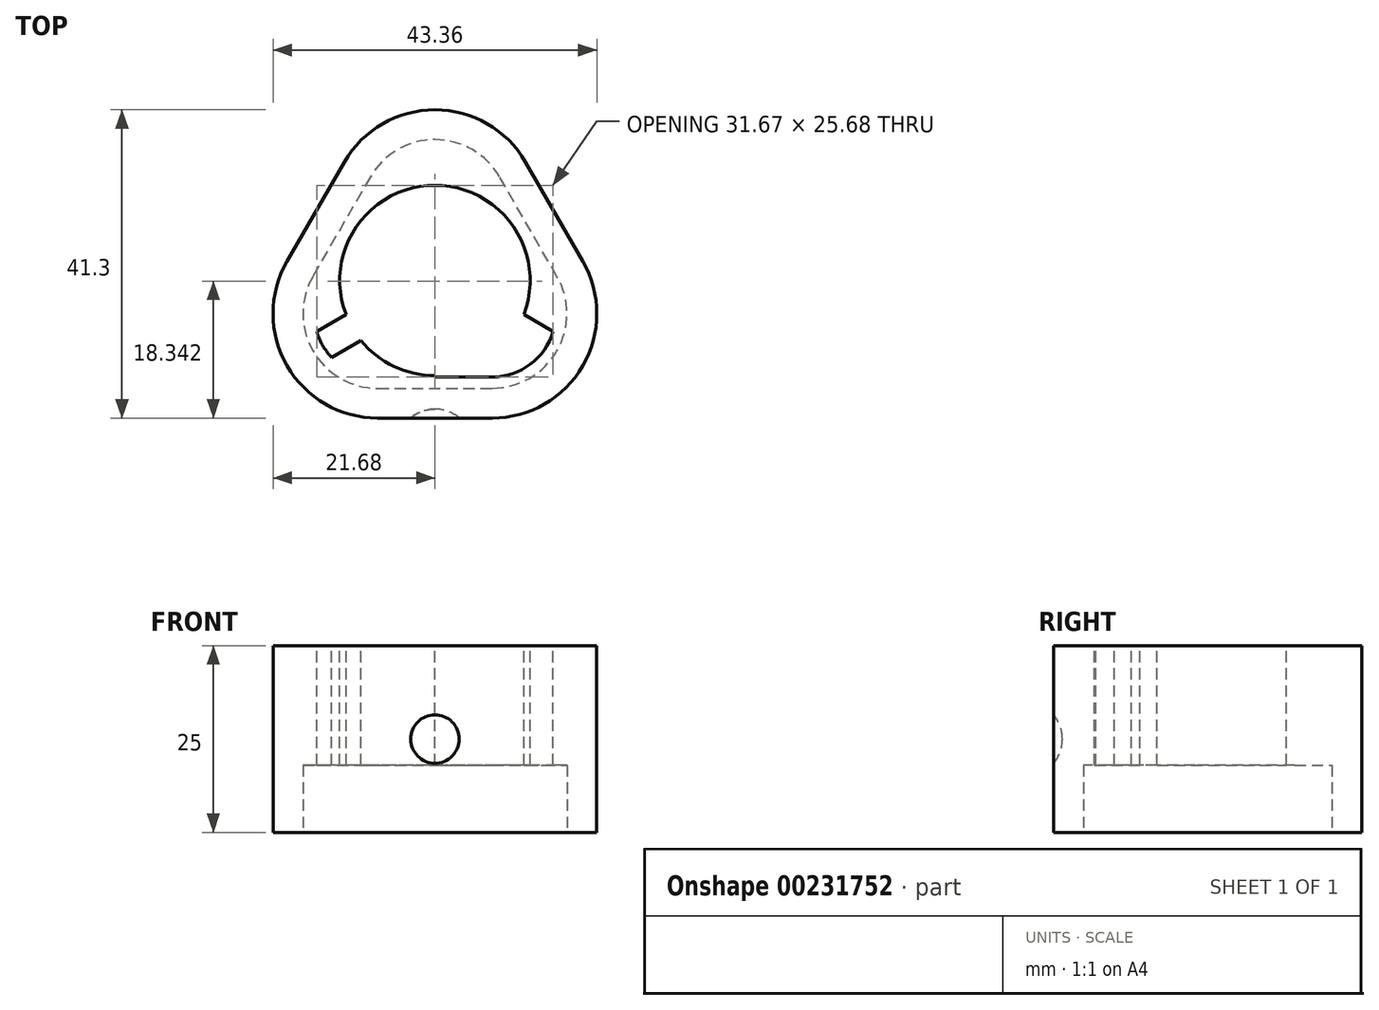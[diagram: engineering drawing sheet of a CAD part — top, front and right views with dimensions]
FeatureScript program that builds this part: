
annotation { "Feature Type Name" : "Feature", "Feature Type Description" : "" }
export const myFeature = defineFeature(function(context is Context, id is Id, definition is map)
    precondition{}
    {
        {
            var Q0;
            Q0=qCreatedBy(makeId("Top.planeOp"),FACE);
            var sketch = newSketch(context, id + "F0", { "sketchPlane" : qUnion([Q0])});
            skLineSegment(sketch, "E0", {"start": v(0, 0) * mm, "end": v(7.68, 0) * mm});
            skLineSegment(sketch, "E1", {"start": v(16.34, 15) * mm, "end": v(8.66, 28.3) * mm});
            skLineSegment(sketch, "E2", {"start": v(-8.66, 28.3) * mm, "end": v(-16.34, 15) * mm});
            skLineSegment(sketch, "E3", {"start": v(-7.68, 0) * mm, "end": v(0, 0) * mm});
            skLineSegment(sketch, "E4", {"start": v(0, 0) * mm, "end": v(0, 43.3) * mm, "construction": true});
            skLineSegment(sketch, "E5", {"start": v(-12.5, 21.65) * mm, "end": v(25, 0) * mm, "construction": true});
            skLineSegment(sketch, "E6", {"start": v(12.5, 21.65) * mm, "end": v(-25, 0) * mm, "construction": true});
            skCircle(sketch, "E7", {"center": v(0, 14.43) * mm, "radius": 12.5 * mm});
            skPoint(sketch, "E8.visualSharp", {"position": v(0, 43.3) * mm});
            skArc(sketch, "E8.filletArc", {"start": v(8.66, 28.3) * mm, "mid": v(0, 33.3) * mm, "end": v(-8.66, 28.3) * mm});
            skPoint(sketch, "E9.visualSharp", {"position": v(-25, 0) * mm});
            skArc(sketch, "E9.filletArc", {"start": v(-16.34, 15) * mm, "mid": v(-16.34, 5) * mm, "end": v(-7.68, 0) * mm});
            skPoint(sketch, "E10.visualSharp", {"position": v(25, 0) * mm});
            skArc(sketch, "E10.filletArc", {"start": v(7.68, 0) * mm, "mid": v(16.34, 5) * mm, "end": v(16.34, 15) * mm});
            skLineSegment(sketch, "E11.0", {"start": v(19.8, 17) * mm, "end": v(12.12, 30.3) * mm});
            skArc(sketch, "E11.1", {"start": v(7.68, -4) * mm, "mid": v(19.8, 3) * mm, "end": v(19.8, 17) * mm});
            skLineSegment(sketch, "E11.2", {"start": v(-12.12, 30.3) * mm, "end": v(-19.8, 17) * mm});
            skArc(sketch, "E11.3", {"start": v(-19.8, 17) * mm, "mid": v(-19.8, 3) * mm, "end": v(-7.68, -4) * mm});
            skLineSegment(sketch, "E11.4", {"start": v(-7.68, -4) * mm, "end": v(0, -4) * mm});
            skArc(sketch, "E11.5", {"start": v(12.12, 30.3) * mm, "mid": v(0, 37.3) * mm, "end": v(-12.12, 30.3) * mm});
            skLineSegment(sketch, "E11.6", {"start": v(0, -4) * mm, "end": v(7.68, -4) * mm});
            skSolve(sketch);
        }
        {
            var Q0;
            Q0=makeQuery(id+"F0.imprint","IMPRINT",FACE,{"disambiguationData":[TD([[makeQuery(id+"F0.imprint","IMPRINT",EDGE,{"derivedFrom":sQuery(id+"F0.wireOp",EDGE,"E0")}),-1.0]])]});
            extrude(context, id + "F1", {"entities" : qUnion([Q0]), "depth" : 25 * mm});
        }
        {
            var Q0;
            Q0=makeQuery(id+"F1.opExtrude","CAP_FACE",FACE,{"disambiguationData":[OSD([sQuery(id+"F0.wireOp",EDGE,"E0"),sQuery(id+"F0.wireOp",EDGE,"E1"),sQuery(id+"F0.wireOp",EDGE,"E2"),sQuery(id+"F0.wireOp",EDGE,"E3"),sQuery(id+"F0.wireOp",EDGE,"E8.filletArc"),sQuery(id+"F0.wireOp",EDGE,"E9.filletArc"),sQuery(id+"F0.wireOp",EDGE,"E10.filletArc"),sQuery(id+"F0.wireOp",EDGE,"E11.0"),sQuery(id+"F0.wireOp",EDGE,"E11.1"),sQuery(id+"F0.wireOp",EDGE,"E11.2"),sQuery(id+"F0.wireOp",EDGE,"E11.3"),sQuery(id+"F0.wireOp",EDGE,"E11.4"),sQuery(id+"F0.wireOp",EDGE,"E11.5"),sQuery(id+"F0.wireOp",EDGE,"E11.6")])],"isStart":false});
            var sketch = newSketch(context, id + "F2", { "sketchPlane" : qUnion([Q0])});
            skLineSegment(sketch, "E12", {"start": v(-12.5, 21.65) * mm, "end": v(16.34, 5) * mm});
            skLineSegment(sketch, "E13", {"start": v(12.5, 21.65) * mm, "end": v(-16.34, 5) * mm});
            skCircle(sketch, "E14", {"center": v(0, 14.43) * mm, "radius": 12.75 * mm});
            skLineSegment(sketch, "E15.0", {"start": v(-8.66, 28.3) * mm, "end": v(-16.34, 15) * mm});
            skArc(sketch, "E16.0", {"start": v(-16.34, 15) * mm, "mid": v(-16.34, 5) * mm, "end": v(-7.68, 0) * mm});
            skLineSegment(sketch, "E17.0", {"start": v(-7.68, 0) * mm, "end": v(7.68, 0) * mm});
            skArc(sketch, "E18.0", {"start": v(7.68, 0) * mm, "mid": v(16.34, 5) * mm, "end": v(16.34, 15) * mm});
            skLineSegment(sketch, "E19.0", {"start": v(16.34, 15) * mm, "end": v(8.66, 28.3) * mm});
            skArc(sketch, "E20.0", {"start": v(8.66, 28.3) * mm, "mid": v(0, 33.3) * mm, "end": v(-8.66, 28.3) * mm});
            skLineSegment(sketch, "E21.0", {"start": v(11.5, 23.38) * mm, "end": v(-17.34, 6.73) * mm});
            skLineSegment(sketch, "E22.0", {"start": v(13.5, 19.92) * mm, "end": v(-15.34, 3.27) * mm});
            skLineSegment(sketch, "E23.0", {"start": v(-13.5, 19.92) * mm, "end": v(15.34, 3.27) * mm});
            skLineSegment(sketch, "E24.0", {"start": v(-11.5, 23.38) * mm, "end": v(17.34, 6.73) * mm});
            skLineSegment(sketch, "E25", {"start": v(0, 0) * mm, "end": v(0, 33.3) * mm});
            skLineSegment(sketch, "E26.0", {"start": v(2, 0) * mm, "end": v(2, 33.3) * mm});
            skLineSegment(sketch, "E27.0", {"start": v(-2, 0) * mm, "end": v(-2, 33.3) * mm});
            skArc(sketch, "E28.0", {"start": v(7.36, 27.55) * mm, "mid": v(0, 31.8) * mm, "end": v(-7.36, 27.55) * mm});
            skArc(sketch, "E28.1", {"start": v(-15.04, 14.25) * mm, "mid": v(-15.04, 5.75) * mm, "end": v(-7.68, 1.5) * mm});
            skLineSegment(sketch, "E28.2", {"start": v(-7.68, 1.5) * mm, "end": v(7.68, 1.5) * mm});
            skLineSegment(sketch, "E28.3", {"start": v(-7.36, 27.55) * mm, "end": v(-15.04, 14.25) * mm});
            skArc(sketch, "E28.4", {"start": v(7.68, 1.5) * mm, "mid": v(15.04, 5.75) * mm, "end": v(15.04, 14.25) * mm});
            skLineSegment(sketch, "E28.5", {"start": v(15.04, 14.25) * mm, "end": v(7.36, 27.55) * mm});
            skSolve(sketch);
        }
        {
            var Q0;
            {var subQ0=sQuery(id+"F2.wireOp",EDGE,"E15.0");var subQ1=sQuery(id+"F2.wireOp",EDGE,"E12");var subQ2=makeQuery(id+"F2.imprint","INTERSECT",VERTEX,{"derivedFrom":[subQ1,subQ0]});Q0=makeQuery(id+"F2.imprint","IMPRINT",FACE,{"disambiguationData":[TD([[makeQuery(id+"F2.imprint","IMPRINT",EDGE,{"disambiguationData":[TD([[subQ2,-1.0]])],"derivedFrom":subQ1}),1.0]])]});}
            var Q1;
            {var subQ0=sQuery(id+"F2.wireOp",EDGE,"E15.0");var subQ1=sQuery(id+"F2.wireOp",EDGE,"E12");var subQ2=makeQuery(id+"F2.imprint","INTERSECT",VERTEX,{"derivedFrom":[subQ1,subQ0]});Q1=makeQuery(id+"F2.imprint","IMPRINT",FACE,{"disambiguationData":[TD([[makeQuery(id+"F2.imprint","IMPRINT",EDGE,{"disambiguationData":[TD([[subQ2,-1.0]])],"derivedFrom":subQ1}),-1.0]])]});}
            var Q2;
            {var subQ0=sQuery(id+"F2.wireOp",EDGE,"E18.0");var subQ1=sQuery(id+"F2.wireOp",EDGE,"E12");var subQ2=makeQuery(id+"F2.imprint","INTERSECT",VERTEX,{"derivedFrom":[subQ1,subQ0]});Q2=makeQuery(id+"F2.imprint","IMPRINT",FACE,{"disambiguationData":[TD([[makeQuery(id+"F2.imprint","IMPRINT",EDGE,{"disambiguationData":[TD([[subQ2,1.0]])],"derivedFrom":subQ1}),-1.0]])]});}
            var Q3;
            {var subQ0=sQuery(id+"F2.wireOp",EDGE,"E18.0");var subQ1=sQuery(id+"F2.wireOp",EDGE,"E12");var subQ2=makeQuery(id+"F2.imprint","INTERSECT",VERTEX,{"derivedFrom":[subQ1,subQ0]});Q3=makeQuery(id+"F2.imprint","IMPRINT",FACE,{"disambiguationData":[TD([[makeQuery(id+"F2.imprint","IMPRINT",EDGE,{"disambiguationData":[TD([[subQ2,1.0]])],"derivedFrom":subQ1}),1.0]])]});}
            var Q4;
            {var subQ0=sQuery(id+"F2.wireOp",EDGE,"E19.0");var subQ1=sQuery(id+"F2.wireOp",EDGE,"E13");var subQ2=makeQuery(id+"F2.imprint","INTERSECT",VERTEX,{"derivedFrom":[subQ1,subQ0]});Q4=makeQuery(id+"F2.imprint","IMPRINT",FACE,{"disambiguationData":[TD([[makeQuery(id+"F2.imprint","IMPRINT",EDGE,{"disambiguationData":[TD([[subQ2,-1.0]])],"derivedFrom":subQ1}),1.0]])]});}
            var Q5;
            {var subQ0=sQuery(id+"F2.wireOp",EDGE,"E19.0");var subQ1=sQuery(id+"F2.wireOp",EDGE,"E13");var subQ2=makeQuery(id+"F2.imprint","INTERSECT",VERTEX,{"derivedFrom":[subQ1,subQ0]});Q5=makeQuery(id+"F2.imprint","IMPRINT",FACE,{"disambiguationData":[TD([[makeQuery(id+"F2.imprint","IMPRINT",EDGE,{"disambiguationData":[TD([[subQ2,-1.0]])],"derivedFrom":subQ1}),-1.0]])]});}
            var Q6;
            {var subQ0=sQuery(id+"F2.wireOp",EDGE,"E16.0");var subQ1=sQuery(id+"F2.wireOp",EDGE,"E13");var subQ2=makeQuery(id+"F2.imprint","INTERSECT",VERTEX,{"derivedFrom":[subQ1,subQ0]});Q6=makeQuery(id+"F2.imprint","IMPRINT",FACE,{"disambiguationData":[TD([[makeQuery(id+"F2.imprint","IMPRINT",EDGE,{"disambiguationData":[TD([[subQ2,1.0]])],"derivedFrom":subQ1}),-1.0]])]});}
            var Q7;
            {var subQ0=sQuery(id+"F2.wireOp",EDGE,"E16.0");var subQ1=sQuery(id+"F2.wireOp",EDGE,"E13");var subQ2=makeQuery(id+"F2.imprint","INTERSECT",VERTEX,{"derivedFrom":[subQ1,subQ0]});Q7=makeQuery(id+"F2.imprint","IMPRINT",FACE,{"disambiguationData":[TD([[makeQuery(id+"F2.imprint","IMPRINT",EDGE,{"disambiguationData":[TD([[subQ2,1.0]])],"derivedFrom":subQ1}),1.0]])]});}
            var Q8;
            {var subQ1=sQuery(id+"F2.wireOp",EDGE,"E20.0");var subQ9=sQuery(id+"F2.wireOp",EDGE,"E15.0");var subQ11=makeQuery(id+"F2.imprint","INTERSECT",VERTEX,{"derivedFrom":[subQ9,subQ1]});Q8=makeQuery(id+"F2.imprint","IMPRINT",FACE,{"disambiguationData":[TD([[makeQuery(id+"F2.imprint","IMPRINT",EDGE,{"disambiguationData":[TD([[subQ11,-1.0]])],"derivedFrom":subQ9}),1.0]])]});}
            var Q9;
            {var subQ1=sQuery(id+"F2.wireOp",EDGE,"E15.0");var subQ9=sQuery(id+"F2.wireOp",EDGE,"E16.0");var subQ11=makeQuery(id+"F2.imprint","INTERSECT",VERTEX,{"derivedFrom":[subQ1,subQ9]});Q9=makeQuery(id+"F2.imprint","IMPRINT",FACE,{"disambiguationData":[TD([[makeQuery(id+"F2.imprint","IMPRINT",EDGE,{"disambiguationData":[TD([[subQ11,1.0]])],"derivedFrom":subQ1}),1.0]])]});}
            var Q10;
            {var subQ1=sQuery(id+"F2.wireOp",EDGE,"E16.0");var subQ5=sQuery(id+"F2.wireOp",EDGE,"E17.0");var subQ6=makeQuery(id+"F2.imprint","INTERSECT",VERTEX,{"derivedFrom":[subQ1,subQ5]});Q10=makeQuery(id+"F2.imprint","IMPRINT",FACE,{"disambiguationData":[TD([[makeQuery(id+"F2.imprint","IMPRINT",EDGE,{"disambiguationData":[TD([[subQ6,1.0]])],"derivedFrom":subQ1}),1.0]])]});}
            var Q11;
            {var subQ0=sQuery(id+"F2.wireOp",EDGE,"E25");var subQ1=sQuery(id+"F2.wireOp",EDGE,"E17.0");var subQ2=makeQuery(id+"F2.imprint","INTERSECT",VERTEX,{"derivedFrom":[subQ1,subQ0]});Q11=makeQuery(id+"F2.imprint","IMPRINT",FACE,{"disambiguationData":[TD([[makeQuery(id+"F2.imprint","IMPRINT",EDGE,{"disambiguationData":[TD([[subQ2,1.0]])],"derivedFrom":subQ1}),1.0]])]});}
            var Q12;
            {var subQ0=sQuery(id+"F2.wireOp",EDGE,"E25");var subQ1=sQuery(id+"F2.wireOp",EDGE,"E17.0");var subQ2=makeQuery(id+"F2.imprint","INTERSECT",VERTEX,{"derivedFrom":[subQ1,subQ0]});Q12=makeQuery(id+"F2.imprint","IMPRINT",FACE,{"disambiguationData":[TD([[makeQuery(id+"F2.imprint","IMPRINT",EDGE,{"disambiguationData":[TD([[subQ2,-1.0]])],"derivedFrom":subQ1}),1.0]])]});}
            var Q13;
            {var subQ1=sQuery(id+"F2.wireOp",EDGE,"E17.0");var subQ9=sQuery(id+"F2.wireOp",EDGE,"E18.0");var subQ10=makeQuery(id+"F2.imprint","INTERSECT",VERTEX,{"derivedFrom":[subQ1,subQ9]});Q13=makeQuery(id+"F2.imprint","IMPRINT",FACE,{"disambiguationData":[TD([[makeQuery(id+"F2.imprint","IMPRINT",EDGE,{"disambiguationData":[TD([[subQ10,1.0]])],"derivedFrom":subQ1}),1.0]])]});}
            var Q14;
            {var subQ1=sQuery(id+"F2.wireOp",EDGE,"E18.0");var subQ6=sQuery(id+"F2.wireOp",EDGE,"E19.0");var subQ10=makeQuery(id+"F2.imprint","INTERSECT",VERTEX,{"derivedFrom":[subQ1,subQ6]});Q14=makeQuery(id+"F2.imprint","IMPRINT",FACE,{"disambiguationData":[TD([[makeQuery(id+"F2.imprint","IMPRINT",EDGE,{"disambiguationData":[TD([[subQ10,1.0]])],"derivedFrom":subQ1}),1.0]])]});}
            var Q15;
            {var subQ1=sQuery(id+"F2.wireOp",EDGE,"E20.0");var subQ6=sQuery(id+"F2.wireOp",EDGE,"E19.0");var subQ10=makeQuery(id+"F2.imprint","INTERSECT",VERTEX,{"derivedFrom":[subQ6,subQ1]});Q15=makeQuery(id+"F2.imprint","IMPRINT",FACE,{"disambiguationData":[TD([[makeQuery(id+"F2.imprint","IMPRINT",EDGE,{"disambiguationData":[TD([[subQ10,1.0]])],"derivedFrom":subQ6}),1.0]])]});}
            var Q16;
            {var subQ0=sQuery(id+"F2.wireOp",EDGE,"E25");var subQ1=sQuery(id+"F2.wireOp",EDGE,"E20.0");var subQ2=makeQuery(id+"F2.imprint","INTERSECT",VERTEX,{"derivedFrom":[subQ1,subQ0]});Q16=makeQuery(id+"F2.imprint","IMPRINT",FACE,{"disambiguationData":[TD([[makeQuery(id+"F2.imprint","IMPRINT",EDGE,{"disambiguationData":[TD([[subQ2,1.0]])],"derivedFrom":subQ1}),1.0]])]});}
            var Q17;
            {var subQ0=sQuery(id+"F2.wireOp",EDGE,"E25");var subQ1=sQuery(id+"F2.wireOp",EDGE,"E20.0");var subQ2=makeQuery(id+"F2.imprint","INTERSECT",VERTEX,{"derivedFrom":[subQ1,subQ0]});Q17=makeQuery(id+"F2.imprint","IMPRINT",FACE,{"disambiguationData":[TD([[makeQuery(id+"F2.imprint","IMPRINT",EDGE,{"disambiguationData":[TD([[subQ2,-1.0]])],"derivedFrom":subQ1}),1.0]])]});}
            var Q18;
            {var subQ5=sQuery(id+"F2.wireOp",EDGE,"E23.0");var subQ6=sQuery(id+"F2.wireOp",EDGE,"E14");var subQ7=makeQuery(id+"F2.imprint","INTERSECT",VERTEX,{"disambiguationData":[OD(0.0)],"derivedFrom":[subQ6,subQ5]});Q18=makeQuery(id+"F2.imprint","IMPRINT",FACE,{"disambiguationData":[TD([[makeQuery(id+"F2.imprint","IMPRINT",EDGE,{"disambiguationData":[TD([[subQ7,-1.0]])],"derivedFrom":subQ6}),-1.0]])]});}
            var Q19;
            {var subQ3=sQuery(id+"F2.wireOp",EDGE,"E22.0");var subQ5=sQuery(id+"F2.wireOp",EDGE,"E14");var subQ6=makeQuery(id+"F2.imprint","INTERSECT",VERTEX,{"disambiguationData":[OD(1.0)],"derivedFrom":[subQ5,subQ3]});Q19=makeQuery(id+"F2.imprint","IMPRINT",FACE,{"disambiguationData":[TD([[makeQuery(id+"F2.imprint","IMPRINT",EDGE,{"disambiguationData":[TD([[subQ6,-1.0]])],"derivedFrom":subQ5}),-1.0]])]});}
            var Q20;
            {var subQ1=sQuery(id+"F2.wireOp",EDGE,"E14");var subQ7=sQuery(id+"F2.wireOp",EDGE,"E26.0");var subQ9=makeQuery(id+"F2.imprint","INTERSECT",VERTEX,{"disambiguationData":[OD(1.0)],"derivedFrom":[subQ1,subQ7]});Q20=makeQuery(id+"F2.imprint","IMPRINT",FACE,{"disambiguationData":[TD([[makeQuery(id+"F2.imprint","IMPRINT",EDGE,{"disambiguationData":[TD([[subQ9,-1.0]])],"derivedFrom":subQ1}),-1.0]])]});}
            var Q21;
            {var subQ5=sQuery(id+"F2.wireOp",EDGE,"E14");var subQ7=sQuery(id+"F2.wireOp",EDGE,"E22.0");var subQ8=makeQuery(id+"F2.imprint","INTERSECT",VERTEX,{"disambiguationData":[OD(0.0)],"derivedFrom":[subQ5,subQ7]});Q21=makeQuery(id+"F2.imprint","IMPRINT",FACE,{"disambiguationData":[TD([[makeQuery(id+"F2.imprint","IMPRINT",EDGE,{"disambiguationData":[TD([[subQ8,1.0]])],"derivedFrom":subQ5}),-1.0]])]});}
            var Q22;
            {var subQ1=sQuery(id+"F2.wireOp",EDGE,"E14");var subQ5=sQuery(id+"F2.wireOp",EDGE,"E21.0");var subQ6=makeQuery(id+"F2.imprint","INTERSECT",VERTEX,{"disambiguationData":[OD(0.0)],"derivedFrom":[subQ1,subQ5]});Q22=makeQuery(id+"F2.imprint","IMPRINT",FACE,{"disambiguationData":[TD([[makeQuery(id+"F2.imprint","IMPRINT",EDGE,{"disambiguationData":[TD([[subQ6,-1.0]])],"derivedFrom":subQ1}),-1.0]])]});}
            var Q23;
            {var subQ0=sQuery(id+"F2.wireOp",EDGE,"E27.0");var subQ1=sQuery(id+"F2.wireOp",EDGE,"E14");var subQ2=makeQuery(id+"F2.imprint","INTERSECT",VERTEX,{"disambiguationData":[OD(0.0)],"derivedFrom":[subQ1,subQ0]});Q23=makeQuery(id+"F2.imprint","IMPRINT",FACE,{"disambiguationData":[TD([[makeQuery(id+"F2.imprint","IMPRINT",EDGE,{"disambiguationData":[TD([[subQ2,-1.0]])],"derivedFrom":subQ1}),-1.0]])]});}
            var Q24;
            {var subQ0=sQuery(id+"F2.wireOp",EDGE,"E28.3");var subQ1=sQuery(id+"F2.wireOp",EDGE,"E12");var subQ2=makeQuery(id+"F2.imprint","INTERSECT",VERTEX,{"derivedFrom":[subQ1,subQ0]});Q24=makeQuery(id+"F2.imprint","IMPRINT",FACE,{"disambiguationData":[TD([[makeQuery(id+"F2.imprint","IMPRINT",EDGE,{"disambiguationData":[TD([[subQ2,-1.0]])],"derivedFrom":subQ1}),1.0]])]});}
            var Q25;
            {var subQ0=sQuery(id+"F2.wireOp",EDGE,"E28.3");var subQ1=sQuery(id+"F2.wireOp",EDGE,"E12");var subQ2=makeQuery(id+"F2.imprint","INTERSECT",VERTEX,{"derivedFrom":[subQ1,subQ0]});Q25=makeQuery(id+"F2.imprint","IMPRINT",FACE,{"disambiguationData":[TD([[makeQuery(id+"F2.imprint","IMPRINT",EDGE,{"disambiguationData":[TD([[subQ2,-1.0]])],"derivedFrom":subQ1}),-1.0]])]});}
            var Q26;
            {var subQ0=sQuery(id+"F2.wireOp",EDGE,"E28.5");var subQ1=sQuery(id+"F2.wireOp",EDGE,"E13");var subQ2=makeQuery(id+"F2.imprint","INTERSECT",VERTEX,{"derivedFrom":[subQ1,subQ0]});Q26=makeQuery(id+"F2.imprint","IMPRINT",FACE,{"disambiguationData":[TD([[makeQuery(id+"F2.imprint","IMPRINT",EDGE,{"disambiguationData":[TD([[subQ2,-1.0]])],"derivedFrom":subQ1}),-1.0]])]});}
            var Q27;
            {var subQ0=sQuery(id+"F2.wireOp",EDGE,"E28.5");var subQ1=sQuery(id+"F2.wireOp",EDGE,"E13");var subQ2=makeQuery(id+"F2.imprint","INTERSECT",VERTEX,{"derivedFrom":[subQ1,subQ0]});Q27=makeQuery(id+"F2.imprint","IMPRINT",FACE,{"disambiguationData":[TD([[makeQuery(id+"F2.imprint","IMPRINT",EDGE,{"disambiguationData":[TD([[subQ2,-1.0]])],"derivedFrom":subQ1}),1.0]])]});}
            var Q28;
            {var subQ0=sQuery(id+"F2.wireOp",EDGE,"E25");var subQ1=sQuery(id+"F2.wireOp",EDGE,"E14");var subQ2=makeQuery(id+"F2.imprint","INTERSECT",VERTEX,{"disambiguationData":[OD(1.0)],"derivedFrom":[subQ1,subQ0]});Q28=makeQuery(id+"F2.imprint","IMPRINT",FACE,{"disambiguationData":[TD([[makeQuery(id+"F2.imprint","IMPRINT",EDGE,{"disambiguationData":[TD([[subQ2,-1.0]])],"derivedFrom":subQ1}),-1.0]])]});}
            var Q29;
            {var subQ0=sQuery(id+"F2.wireOp",EDGE,"E27.0");var subQ1=sQuery(id+"F2.wireOp",EDGE,"E14");var subQ2=makeQuery(id+"F2.imprint","INTERSECT",VERTEX,{"disambiguationData":[OD(1.0)],"derivedFrom":[subQ1,subQ0]});Q29=makeQuery(id+"F2.imprint","IMPRINT",FACE,{"disambiguationData":[TD([[makeQuery(id+"F2.imprint","IMPRINT",EDGE,{"disambiguationData":[TD([[subQ2,-1.0]])],"derivedFrom":subQ1}),-1.0]])]});}
            extrude(context, id + "F3", {"entities" : qUnion([Q0, Q1, Q2, Q3, Q4, Q5, Q6, Q7, Q8, Q9, Q10, Q11, Q12, Q13, Q14, Q15, Q16, Q17, Q18, Q19, Q20, Q21, Q22, Q23, Q24, Q25, Q26, Q27, Q28, Q29]), "operationType" : NewBodyOperationType.ADD, "oppositeDirection" : true, "depth" : 16 * mm});
        }
        {
            var Q0;
            Q0=qCreatedBy(makeId("Top.planeOp"),FACE);
            cPlane(context, id + "F4", {"entities" : qUnion([Q0]), "cplaneType" : CPlaneType.OFFSET, "offset" : 12.5 * mm, "width" : 150 * mm, "height" : 150 * mm});
        }
        {
            var Q0;
            Q0=qCreatedBy(id+"F4.planeOp",FACE);
            var sketch = newSketch(context, id + "F5", { "sketchPlane" : qUnion([Q0])});
            skCircle(sketch, "E29", {"center": v(0, -7.8) * mm, "radius": 5 * mm});
            skLineSegment(sketch, "E30", {"start": v(0, -12.8) * mm, "end": v(0, -2.8) * mm});
            skSolve(sketch);
        }
        {
            var Q0;
            {var subQ0=sQuery(id+"F5.wireOp",EDGE,"E30");Q0=makeQuery(id+"F5.imprint","IMPRINT",FACE,{"disambiguationData":[TD([[makeQuery(id+"F5.imprint","IMPRINT",EDGE,{"derivedFrom":subQ0}),-1.0]])]});}
            var Q1;
            Q1=sQuery(id+"F5.wireOp",EDGE,"E30");
            revolve(context, id + "F6", {"operationType" : NewBodyOperationType.REMOVE, "entities" : qUnion([Q0]), "axis" : qUnion([Q1]), "revolveType" : RevolveType.FULL, "oppositeDirection" : true});
        }
    });
